# Revit family: Plymold-Aurora-Freestanding-Outdoor_Table
name_source: partatom
category: Furniture
units: mm (PartAtom-declared; Revit-internal decimal feet)

## family parameters
Always vertical = Yes
Cut with Voids When Loaded = No
OmniClass Number = 23.40.20.00
OmniClass Title = General Furniture and Specialties
Render Appearance Source = Family Geometry
Room Calculation Point = No
Shared = No
Work Plane-Based = No

## types (8) — shared parameters
Assembly Code = E2020200
Default Elevation = 0"
GLIDES MATERIAL = PLY - Plastic Black
Height = 30"
Keynote = 12500
Manufacturer = Plymold Inc.
Product Documentation Link = https://plymold.com
Revit File Built By = https://servex-us.com
Sustainability = https://plymold.com
TOP MATERIAL = PLY - Sand
Type Comments = Aurora
URL = https://plymold.com

## per-type parameters (varying)
| type | Depth | Description | FRAME MATERIAL | SUPPORT MATERIAL | Su | Width |
| 26030030PL03 | 26" | Freestanding Table - Onyx Black - 30"W x 26"D x 30"H | PLY - Onyx Black Powdercoat | PLY - Onyx Black Powdercoat | No | 30" |
| 26044030PL03 | 26" | Freestanding Table - Onyx Black - 44"W x 26"D x 30"H | PLY - Onyx Black Powdercoat | PLY - Onyx Black Powdercoat | Yes | 44" |
| 37537530PL03 | 37 1/2" | Freestanding Table - Onyx Black - 37 .5"W x 37.5"D x 30"H | PLY - Onyx Black Powdercoat | PLY - Onyx Black Powdercoat | No | 37 1/2" |
| 37557030PL03 | 37 1/2" | Freestanding Table - Onyx Black - 57"W x 37.5"D x 30"H | PLY - Onyx Black Powdercoat | PLY - Onyx Black Powdercoat | Yes | 57" |
| 26030030PL02 | 26" | Freestanding Table - Iron Glimme - 30"W x 26"D x 30"H | PLY - Iron Glimme Powdercoat | PLY - Iron Glimme Powdercoat | No | 30" |
| 26044030PL02 | 26" | Freestanding Table - Iron Glimme - 44"W x 26"D x 30"H | PLY - Iron Glimme Powdercoat | PLY - Iron Glimme Powdercoat | Yes | 44" |
| 37537530PL02 | 37 1/2" | Freestanding Table - Iron Glimme - 37 .5"W x 37.5"D x 30"H | PLY - Iron Glimme Powdercoat | PLY - Iron Glimme Powdercoat | No | 37 1/2" |
| 37557030PL02 | 37 1/2" | Freestanding Table - Iron Glimme - 57"W x 37.5"D x 30"H | PLY - Iron Glimme Powdercoat | PLY - Iron Glimme Powdercoat | Yes | 57" |

note: column(s) folded — value = type name in every type: Model

## geometry (parser evidence)
native form markers: Sweep x4
no freeform markers — native parametric forms only
